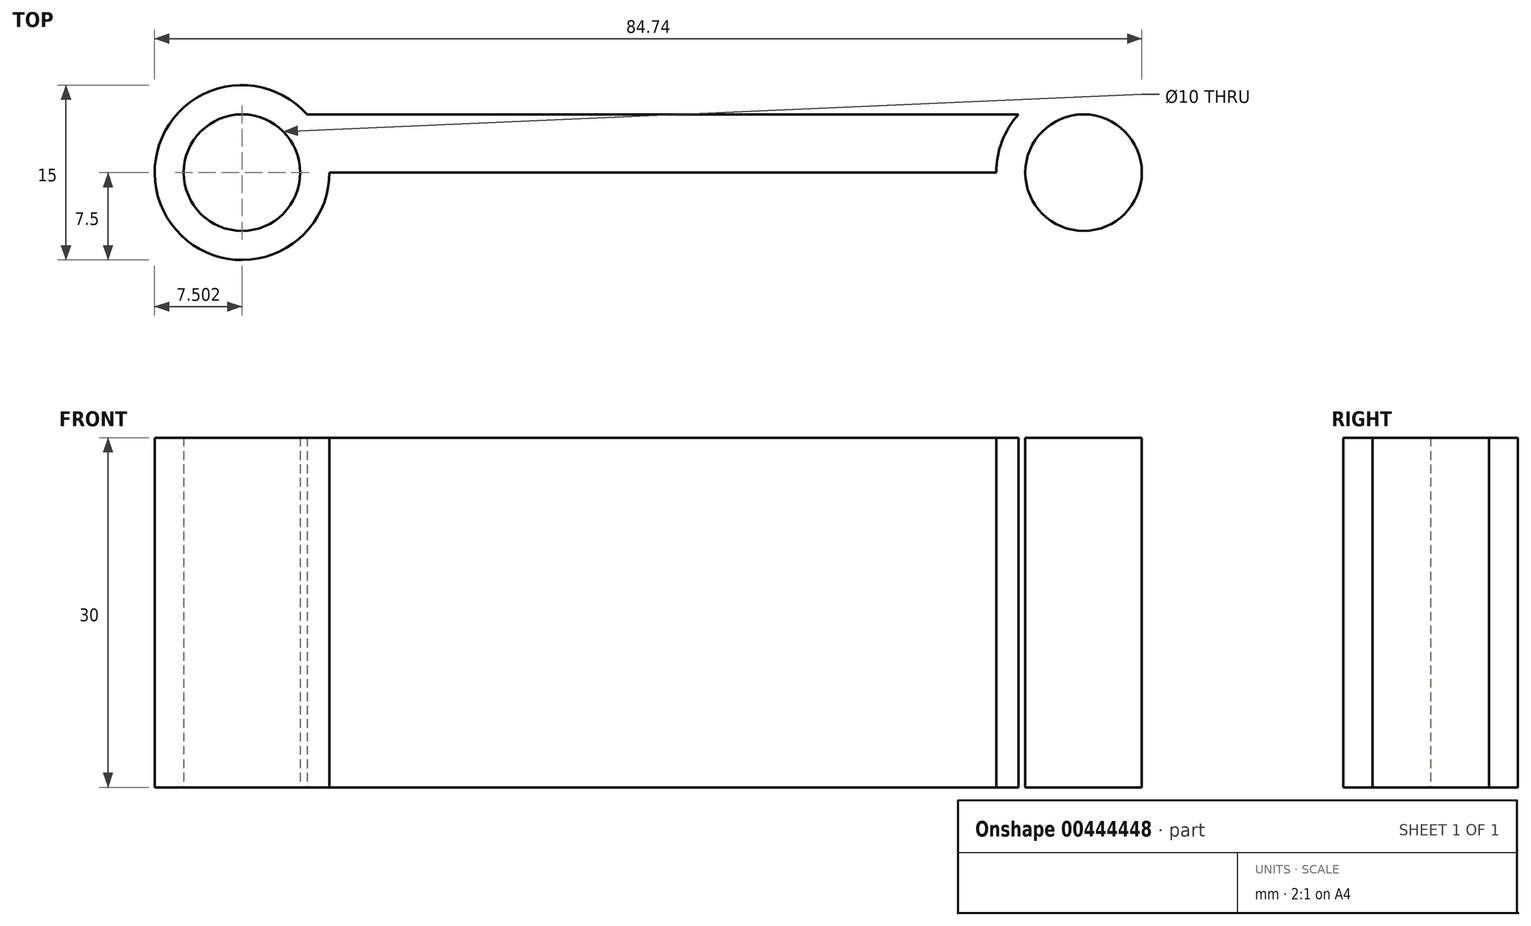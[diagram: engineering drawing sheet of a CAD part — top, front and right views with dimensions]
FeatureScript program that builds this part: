
annotation { "Feature Type Name" : "Feature", "Feature Type Description" : "" }
export const myFeature = defineFeature(function(context is Context, id is Id, definition is map)
    precondition{}
    {
        {
            var Q0;
            Q0=qCreatedBy(makeId("Top.planeOp"),FACE);
            var sketch = newSketch(context, id + "F0", { "sketchPlane" : qUnion([Q0])});
            skCircle(sketch, "E0", {"center": v(-36.12, 0) * mm, "radius": 5 * mm});
            skCircle(sketch, "E1", {"center": v(-36.12, 0) * mm, "radius": 7.5 * mm});
            skCircle(sketch, "E2.MirrorC", {"center": v(36.12, 0) * mm, "radius": 5 * mm});
            skCircle(sketch, "E3.MirrorC", {"center": v(36.12, 0) * mm, "radius": 7.5 * mm});
            skLineSegment(sketch, "E4", {"start": v(-30.53, 5) * mm, "end": v(30.53, 5) * mm});
            skLineSegment(sketch, "E5", {"start": v(28.62, 0) * mm, "end": v(-28.62, 0) * mm});
            skSolve(sketch);
        }
        {
            var Q0;
            Q0=makeQuery(id+"F0.imprint","IMPRINT",FACE,{"disambiguationData":[TD([[makeQuery(id+"F0.imprint","IMPRINT",EDGE,{"derivedFrom":sQuery(id+"F0.wireOp",EDGE,"E0")}),-1.0]])]});
            var Q1;
            {var subQ0=sQuery(id+"F0.wireOp",EDGE,"E4");Q1=makeQuery(id+"F0.imprint","IMPRINT",FACE,{"disambiguationData":[TD([[makeQuery(id+"F0.imprint","IMPRINT",EDGE,{"derivedFrom":subQ0}),-1.0]])]});}
            var Q2;
            Q2=makeQuery(id+"F0.imprint","IMPRINT",FACE,{"disambiguationData":[TD([[makeQuery(id+"F0.imprint","IMPRINT",EDGE,{"derivedFrom":sQuery(id+"F0.wireOp",EDGE,"E2.MirrorC")}),1.0]])]});
            extrude(context, id + "F1", {"entities" : qUnion([Q0, Q1, Q2]), "depth" : 30 * mm});
        }
    });
